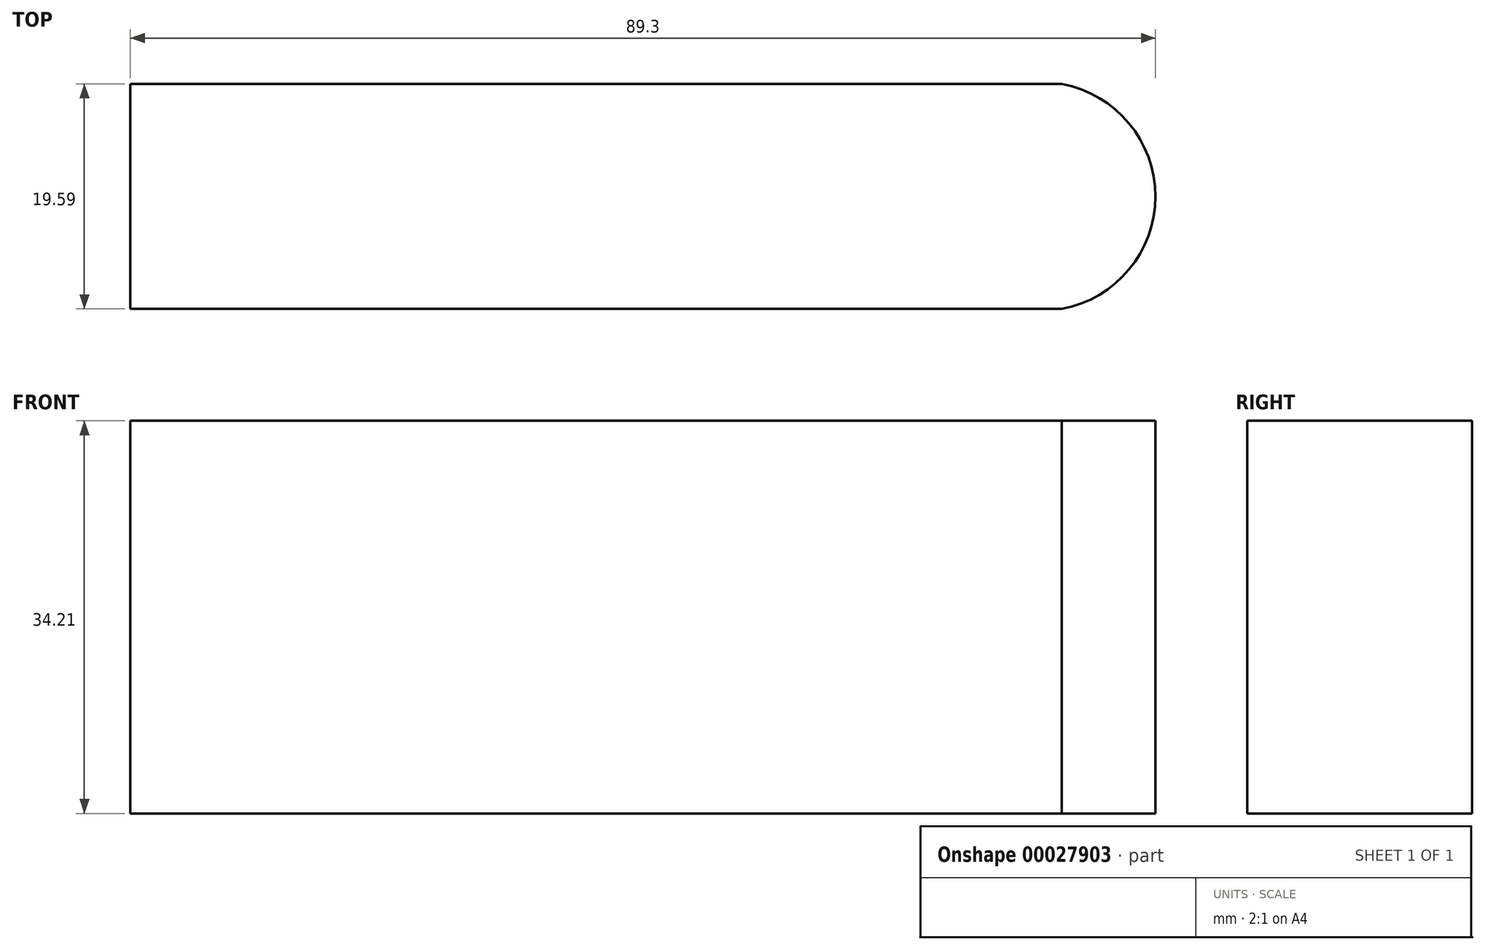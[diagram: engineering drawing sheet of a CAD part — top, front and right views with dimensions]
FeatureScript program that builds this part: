
annotation { "Feature Type Name" : "Feature", "Feature Type Description" : "" }
export const myFeature = defineFeature(function(context is Context, id is Id, definition is map)
    precondition{}
    {
        {
            var Q0;
            Q0=qCreatedBy(makeId("Top.planeOp"),FACE);
            var sketch = newSketch(context, id + "F0", { "sketchPlane" : qUnion([Q0])});
            skLineSegment(sketch, "E0.rect.bottom", {"start": v(40.57, 9.8) * mm, "end": v(-40.57, 9.8) * mm});
            skLineSegment(sketch, "E0.rect.top", {"start": v(40.57, -9.8) * mm, "end": v(-40.57, -9.8) * mm});
            skLineSegment(sketch, "E0.rect.left", {"start": v(40.57, 9.8) * mm, "end": v(40.57, -9.8) * mm});
            skLineSegment(sketch, "E0.rect.right", {"start": v(-40.57, 9.8) * mm, "end": v(-40.57, -9.8) * mm});
            skPoint(sketch, "E0.rect.middle", {"position": v(0, 0) * mm});
            skArc(sketch, "E1", {"start": v(40.57, -9.8) * mm, "mid": v(48.73, 0) * mm, "end": v(40.57, 9.8) * mm});
            skSolve(sketch);
        }
        {
            var Q0;
            Q0=makeQuery(id+"F0.imprint","IMPRINT",FACE,{"disambiguationData":[TD([[makeQuery(id+"F0.imprint","IMPRINT",EDGE,{"derivedFrom":sQuery(id+"F0.wireOp",EDGE,"E0.rect.bottom")}),1.0]])]});
            var Q1;
            Q1=makeQuery(id+"F0.imprint","IMPRINT",FACE,{"disambiguationData":[TD([[makeQuery(id+"F0.imprint","IMPRINT",EDGE,{"derivedFrom":sQuery(id+"F0.wireOp",EDGE,"E0.rect.left")}),1.0]])]});
            extrude(context, id + "F1", {"entities" : qUnion([Q0, Q1]), "depth" : 34.2 * mm});
        }
    });
